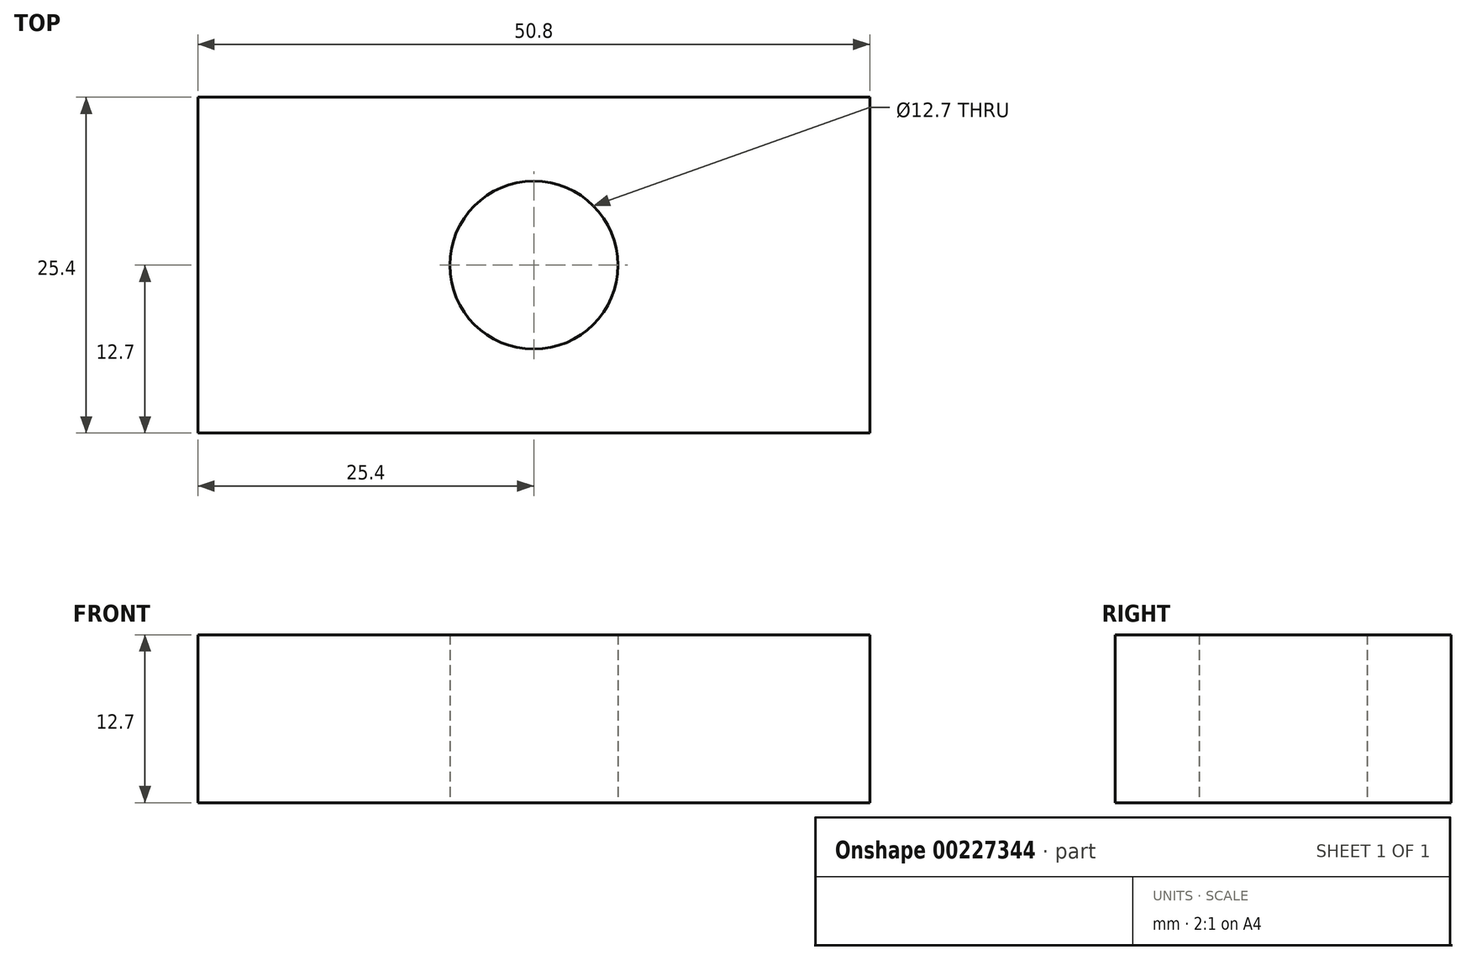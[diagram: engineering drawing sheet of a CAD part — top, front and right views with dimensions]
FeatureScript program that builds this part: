
annotation { "Feature Type Name" : "Feature", "Feature Type Description" : "" }
export const myFeature = defineFeature(function(context is Context, id is Id, definition is map)
    precondition{}
    {
        {
            var Q0;
            Q0=qCreatedBy(makeId("Top.planeOp"),FACE);
            var sketch = newSketch(context, id + "F0", { "sketchPlane" : qUnion([Q0])});
            skLineSegment(sketch, "E0.bottom", {"start": v(0, 0) * mm, "end": v(50.8, 0) * mm});
            skLineSegment(sketch, "E0.top", {"start": v(0, -25.4) * mm, "end": v(50.8, -25.4) * mm});
            skLineSegment(sketch, "E0.left", {"start": v(0, 0) * mm, "end": v(0, -25.4) * mm});
            skLineSegment(sketch, "E0.right", {"start": v(50.8, 0) * mm, "end": v(50.8, -25.4) * mm});
            skCircle(sketch, "E1", {"center": v(25.4, -12.7) * mm, "radius": 6.35 * mm});
            skLineSegment(sketch, "E2", {"start": v(25.4, -12.7) * mm, "end": v(25.4, -25.4) * mm, "construction": true});
            skLineSegment(sketch, "E3", {"start": v(1, -12.7) * mm, "end": v(25.4, -12.7) * mm, "construction": true});
            skPoint(sketch, "E3.startSnap0", {"position": v(0, -12.7) * mm});
            skSolve(sketch);
        }
        {
            var Q0;
            Q0 = qSketchRegion(id + "F0", true);
            extrude(context, id + "F1", {"entities" : qUnion([Q0]), "depth" : 12.7 * mm});
        }
    });
